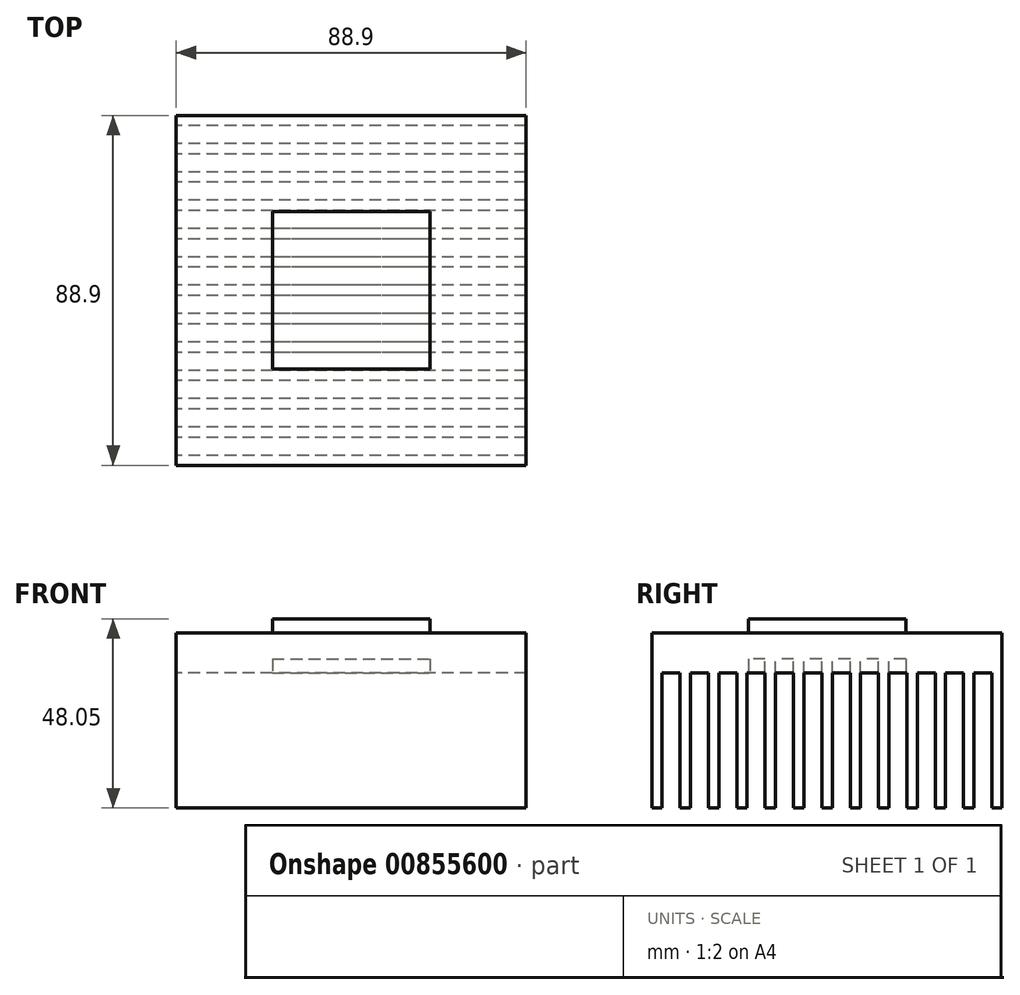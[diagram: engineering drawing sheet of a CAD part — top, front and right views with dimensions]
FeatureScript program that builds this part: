
annotation { "Feature Type Name" : "Feature", "Feature Type Description" : "" }
export const myFeature = defineFeature(function(context is Context, id is Id, definition is map)
    precondition{}
    {
        {
            var Q0;
            Q0=qCreatedBy(makeId("Top.planeOp"),FACE);
            var sketch = newSketch(context, id + "F0", { "sketchPlane" : qUnion([Q0])});
            skLineSegment(sketch, "E0.bottom", {"start": v(-37.26, 47.83) * mm, "end": v(51.64, 47.83) * mm});
            skLineSegment(sketch, "E0.top", {"start": v(-37.26, -41.07) * mm, "end": v(51.64, -41.07) * mm});
            skLineSegment(sketch, "E0.left", {"start": v(-37.26, 47.83) * mm, "end": v(-37.26, -41.07) * mm});
            skLineSegment(sketch, "E0.right", {"start": v(51.64, 47.83) * mm, "end": v(51.64, -41.07) * mm});
            skSolve(sketch);
        }
        {
            var Q0;
            Q0 = qSketchRegion(id + "F0", true);
            extrude(context, id + "F1", {"entities" : qUnion([Q0]), "depth" : 44.45 * mm, "offsetDistance" : 25.4 * mm});
        }
        {
            var Q0;
            Q0=makeQuery(id+"F1.opExtrude","CAP_FACE",FACE,{"disambiguationData":[OSD([sQuery(id+"F0.wireOp",EDGE,"E0.bottom"),sQuery(id+"F0.wireOp",EDGE,"E0.top"),sQuery(id+"F0.wireOp",EDGE,"E0.left"),sQuery(id+"F0.wireOp",EDGE,"E0.right")])],"isStart":false});
            var sketch = newSketch(context, id + "F2", { "sketchPlane" : qUnion([Q0])});
            skLineSegment(sketch, "E1.bottom", {"start": v(-12.81, 23.38) * mm, "end": v(27.19, 23.38) * mm});
            skLineSegment(sketch, "E1.top", {"start": v(-12.81, -16.62) * mm, "end": v(27.19, -16.62) * mm});
            skLineSegment(sketch, "E1.left", {"start": v(-12.81, 23.38) * mm, "end": v(-12.81, -16.62) * mm});
            skLineSegment(sketch, "E1.right", {"start": v(27.19, 23.38) * mm, "end": v(27.19, -16.62) * mm});
            skPoint(sketch, "E2", {"position": v(7.19, 47.83) * mm});
            skPoint(sketch, "E3", {"position": v(-37.26, 3.38) * mm});
            skPoint(sketch, "E4", {"position": v(-12.81, 3.38) * mm});
            skPoint(sketch, "E5", {"position": v(7.19, 23.38) * mm});
            skLineSegment(sketch, "E6", {"start": v(7.19, 47.83) * mm, "end": v(7.19, 68.84) * mm, "construction": true});
            skLineSegment(sketch, "E7", {"start": v(7.19, 17.53) * mm, "end": v(7.19, 23.38) * mm, "construction": true});
            skLineSegment(sketch, "E8", {"start": v(-12.81, 3.38) * mm, "end": v(-27.5, 3.38) * mm, "construction": true});
            skLineSegment(sketch, "E9", {"start": v(-37.26, 3.38) * mm, "end": v(-50.14, 3.38) * mm, "construction": true});
            skSolve(sketch);
        }
        {
            var Q0;
            Q0 = qSketchRegion(id + "F2", true);
            extrude(context, id + "F3", {"entities" : qUnion([Q0]), "operationType" : NewBodyOperationType.ADD, "depth" : 3.6 * mm, "offsetDistance" : 25.4 * mm});
        }
        {
            var Q0;
            Q0=makeQuery(id+"F1.opExtrude","CAP_FACE",FACE,{"disambiguationData":[OSD([sQuery(id+"F0.wireOp",EDGE,"E0.bottom"),sQuery(id+"F0.wireOp",EDGE,"E0.top"),sQuery(id+"F0.wireOp",EDGE,"E0.left"),sQuery(id+"F0.wireOp",EDGE,"E0.right")])],"isStart":true});
            var sketch = newSketch(context, id + "F4", { "sketchPlane" : qUnion([Q0])});
            skLineSegment(sketch, "E10.bottom", {"start": v(51.64, 38.53) * mm, "end": v(-37.26, 38.53) * mm});
            skLineSegment(sketch, "E10.top", {"start": v(51.64, 33.96) * mm, "end": v(-37.26, 33.96) * mm});
            skLineSegment(sketch, "E10.left", {"start": v(51.64, 38.53) * mm, "end": v(51.64, 33.96) * mm});
            skLineSegment(sketch, "E10.right", {"start": v(-37.26, 38.53) * mm, "end": v(-37.26, 33.96) * mm});
            skLineSegment(sketch, "E11.0.1.0", {"start": v(51.64, 26.76) * mm, "end": v(-37.26, 26.76) * mm});
            skLineSegment(sketch, "E11.0.1.1", {"start": v(51.64, 31.33) * mm, "end": v(-37.26, 31.33) * mm});
            skLineSegment(sketch, "E11.0.1.2", {"start": v(51.64, 31.33) * mm, "end": v(51.64, 26.76) * mm});
            skLineSegment(sketch, "E11.0.1.3", {"start": v(-37.26, 31.33) * mm, "end": v(-37.26, 26.76) * mm});
            skLineSegment(sketch, "E11.0.2.0", {"start": v(51.64, 19.55) * mm, "end": v(-37.26, 19.55) * mm});
            skLineSegment(sketch, "E11.0.2.1", {"start": v(51.64, 24.12) * mm, "end": v(-37.26, 24.12) * mm});
            skLineSegment(sketch, "E11.0.2.2", {"start": v(51.64, 24.12) * mm, "end": v(51.64, 19.55) * mm});
            skLineSegment(sketch, "E11.0.2.3", {"start": v(-37.26, 24.12) * mm, "end": v(-37.26, 19.55) * mm});
            skLineSegment(sketch, "E11.0.3.0", {"start": v(51.64, 12.35) * mm, "end": v(-37.26, 12.35) * mm});
            skLineSegment(sketch, "E11.0.3.1", {"start": v(51.64, 16.92) * mm, "end": v(-37.26, 16.92) * mm});
            skLineSegment(sketch, "E11.0.3.2", {"start": v(51.64, 16.92) * mm, "end": v(51.64, 12.35) * mm});
            skLineSegment(sketch, "E11.0.3.3", {"start": v(-37.26, 16.92) * mm, "end": v(-37.26, 12.35) * mm});
            skLineSegment(sketch, "E11.0.4.0", {"start": v(51.64, 5.14) * mm, "end": v(-37.26, 5.14) * mm});
            skLineSegment(sketch, "E11.0.4.1", {"start": v(51.64, 9.72) * mm, "end": v(-37.26, 9.72) * mm});
            skLineSegment(sketch, "E11.0.4.2", {"start": v(51.64, 9.72) * mm, "end": v(51.64, 5.14) * mm});
            skLineSegment(sketch, "E11.0.4.3", {"start": v(-37.26, 9.72) * mm, "end": v(-37.26, 5.14) * mm});
            skLineSegment(sketch, "E11.0.5.0", {"start": v(51.64, -2.06) * mm, "end": v(-37.26, -2.06) * mm});
            skLineSegment(sketch, "E11.0.5.1", {"start": v(51.64, 2.51) * mm, "end": v(-37.26, 2.51) * mm});
            skLineSegment(sketch, "E11.0.5.2", {"start": v(51.64, 2.51) * mm, "end": v(51.64, -2.06) * mm});
            skLineSegment(sketch, "E11.0.5.3", {"start": v(-37.26, 2.51) * mm, "end": v(-37.26, -2.06) * mm});
            skLineSegment(sketch, "E11.0.6.0", {"start": v(51.64, -9.26) * mm, "end": v(-37.26, -9.26) * mm});
            skLineSegment(sketch, "E11.0.6.1", {"start": v(51.64, -4.7) * mm, "end": v(-37.26, -4.7) * mm});
            skLineSegment(sketch, "E11.0.6.2", {"start": v(51.64, -4.7) * mm, "end": v(51.64, -9.26) * mm});
            skLineSegment(sketch, "E11.0.6.3", {"start": v(-37.26, -4.7) * mm, "end": v(-37.26, -9.26) * mm});
            skLineSegment(sketch, "E11.0.7.0", {"start": v(51.64, -16.47) * mm, "end": v(-37.26, -16.47) * mm});
            skLineSegment(sketch, "E11.0.7.1", {"start": v(51.64, -11.9) * mm, "end": v(-37.26, -11.9) * mm});
            skLineSegment(sketch, "E11.0.7.2", {"start": v(51.64, -11.9) * mm, "end": v(51.64, -16.47) * mm});
            skLineSegment(sketch, "E11.0.7.3", {"start": v(-37.26, -11.9) * mm, "end": v(-37.26, -16.47) * mm});
            skLineSegment(sketch, "E11.0.8.0", {"start": v(51.64, -23.67) * mm, "end": v(-37.26, -23.67) * mm});
            skLineSegment(sketch, "E11.0.8.1", {"start": v(51.64, -19.1) * mm, "end": v(-37.26, -19.1) * mm});
            skLineSegment(sketch, "E11.0.8.2", {"start": v(51.64, -19.1) * mm, "end": v(51.64, -23.67) * mm});
            skLineSegment(sketch, "E11.0.8.3", {"start": v(-37.26, -19.1) * mm, "end": v(-37.26, -23.67) * mm});
            skLineSegment(sketch, "E11.0.9.0", {"start": v(51.64, -30.88) * mm, "end": v(-37.26, -30.88) * mm});
            skLineSegment(sketch, "E11.0.9.1", {"start": v(51.64, -26.3) * mm, "end": v(-37.26, -26.3) * mm});
            skLineSegment(sketch, "E11.0.9.2", {"start": v(51.64, -26.3) * mm, "end": v(51.64, -30.88) * mm});
            skLineSegment(sketch, "E11.0.9.3", {"start": v(-37.26, -26.3) * mm, "end": v(-37.26, -30.88) * mm});
            skLineSegment(sketch, "E11.0.10.0", {"start": v(51.64, -38.08) * mm, "end": v(-37.26, -38.08) * mm});
            skLineSegment(sketch, "E11.0.10.1", {"start": v(51.64, -33.51) * mm, "end": v(-37.26, -33.51) * mm});
            skLineSegment(sketch, "E11.0.10.2", {"start": v(51.64, -33.51) * mm, "end": v(51.64, -38.08) * mm});
            skLineSegment(sketch, "E11.0.10.3", {"start": v(-37.26, -33.51) * mm, "end": v(-37.26, -38.08) * mm});
            skLineSegment(sketch, "E11.0.11.0", {"start": v(51.64, -45.29) * mm, "end": v(-37.26, -45.29) * mm});
            skLineSegment(sketch, "E11.0.11.1", {"start": v(51.64, -40.71) * mm, "end": v(-37.26, -40.71) * mm});
            skLineSegment(sketch, "E11.0.11.2", {"start": v(51.64, -40.71) * mm, "end": v(51.64, -45.29) * mm});
            skLineSegment(sketch, "E11.0.11.3", {"start": v(-37.26, -40.71) * mm, "end": v(-37.26, -45.29) * mm});
            skLineSegment(sketch, "E11.direction1", {"start": v(-37.26, 33.96) * mm, "end": v(-11.35, 33.96) * mm, "construction": true});
            skLineSegment(sketch, "E11.direction2", {"start": v(-37.26, 33.96) * mm, "end": v(-37.26, 26.76) * mm, "construction": true});
            skSolve(sketch);
        }
        {
            var Q0;
            Q0 = qSketchRegion(id + "F4", true);
            extrude(context, id + "F5", {"entities" : qUnion([Q0]), "operationType" : NewBodyOperationType.REMOVE, "endBound" : BoundingType.UP_TO_NEXT, "oppositeDirection" : true, "depth" : 25.4 * mm, "hasOffset" : true, "offsetDistance" : 10.16 * mm});
        }
    });
